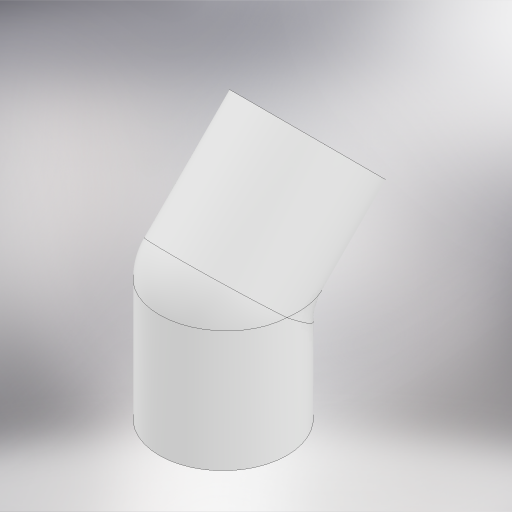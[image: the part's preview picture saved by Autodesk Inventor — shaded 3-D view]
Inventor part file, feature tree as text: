
AUTODESK INVENTOR PART (.ipt)
format: ipt  version: 2023 (Build 270158000, 158)  size: 346,112 bytes
history: native  units: in
note: dims shown in document units (in); Inventor stores cm internally (conversion verified against a paired STEP export)
features: sketch x3, revolve x2, extrude x2, other x1, plane x1, fillet x1
ambient origin geometry x8: Origin, YZ Plane, XZ Plane, XY Plane, X Axis, Y Axis, Z Axis, Center Point
bodies: Body1 (feature_tree)
feature tree (10):
  other  "Sólido1"
  sketch  "Boceto1"  dims[d0=1.2165in d1=0.0in]
  revolve  "Revolución1"  [1 undecoded]
  revolve  "Revolución2"  Angle=135.0deg
  plane  "Plano de trabajo1"
  sketch  "Boceto6"  dims[d2=1.2165in d3=135.0deg]
  sketch  "Boceto7"  dims[d4=0.5246in d5=0.5246in d6=0.6496in d7=0.6496in d8=90.0deg d9=90.0deg d23=0.3937in d24=0.0in d25=0.3937in d26=0.0in d27=0.5906in]
  extrude  "Extrusión3"  Depth=0.5246in
  extrude  "Extrusión4"  Depth=0.6496in
  fillet  "Empalme1"  Radius=0.6496in
note: 1 required parameter value undecoded (feature->parameter linkage not recoverable at this tier; creation-order binding heuristic only, values carry confidence <= 0.55)
